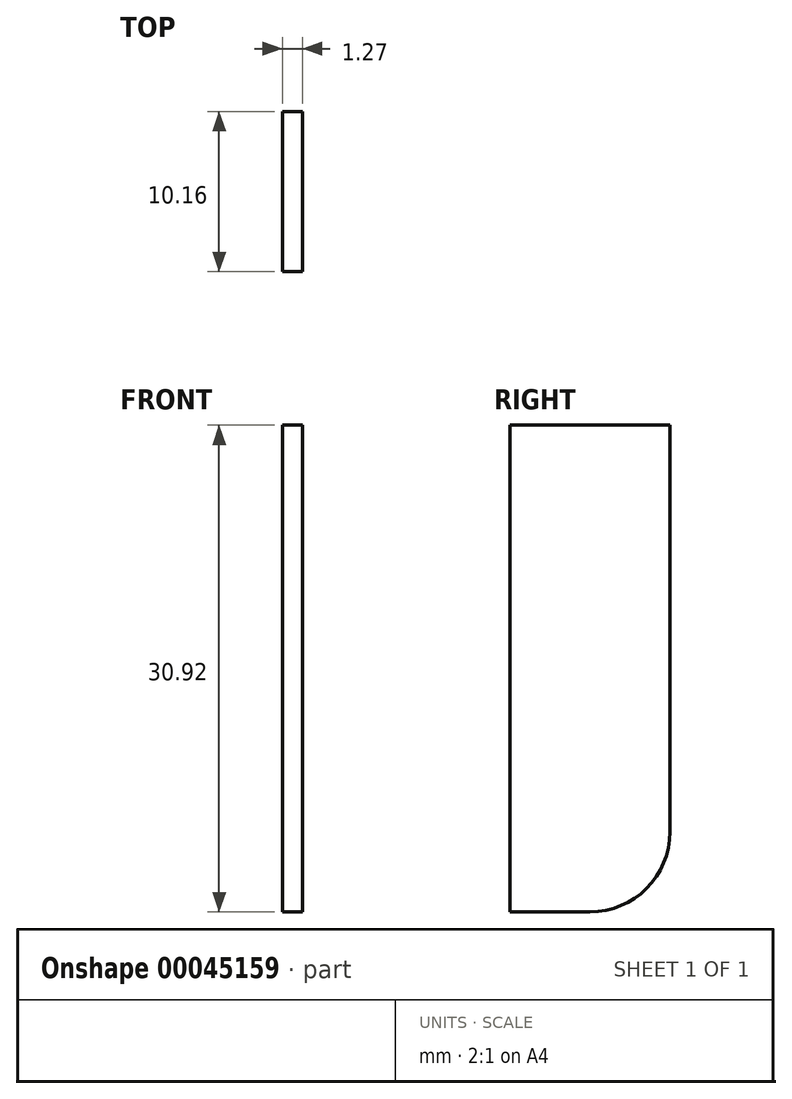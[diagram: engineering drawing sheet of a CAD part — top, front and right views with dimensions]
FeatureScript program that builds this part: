
annotation { "Feature Type Name" : "Feature", "Feature Type Description" : "" }
export const myFeature = defineFeature(function(context is Context, id is Id, definition is map)
    precondition{}
    {
        {
            var Q0;
            Q0=qCreatedBy(makeId("Front.planeOp"),FACE);
            var sketch = newSketch(context, id + "F0", { "sketchPlane" : qUnion([Q0])});
            skLineSegment(sketch, "E0", {"start": v(0, 0) * mm, "end": v(0, 30.92) * mm});
            skLineSegment(sketch, "E1", {"start": v(0, 30.92) * mm, "end": v(1.27, 30.92) * mm});
            skLineSegment(sketch, "E2", {"start": v(1.27, 30.92) * mm, "end": v(1.27, 0) * mm});
            skLineSegment(sketch, "E3", {"start": v(1.27, 0) * mm, "end": v(0, 0) * mm});
            skSolve(sketch);
        }
        {
            var Q0;
            Q0 = qSketchRegion(id + "F0", true);
            extrude(context, id + "F1", {"entities" : qUnion([Q0]), "depth" : 10.16 * mm});
        }
        {
            var Q0;
            Q0=makeQuery(id+"F1.opExtrude","CAP_EDGE",EDGE,{"disambiguationData":[OSD([sQuery(id+"F0.wireOp",EDGE,"E3")])],"isStart":true});
            fillet(context, id + "F2", {"entities" : qUnion([Q0]), "radius" : 5.08 * mm, "tangentPropagation" : true, "allowEdgeOverflow" : false});
        }
    });
